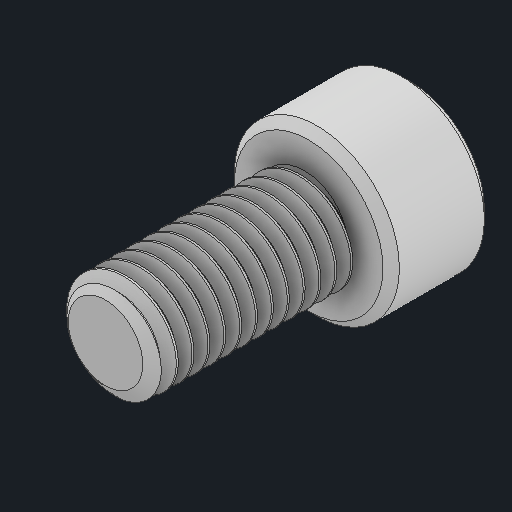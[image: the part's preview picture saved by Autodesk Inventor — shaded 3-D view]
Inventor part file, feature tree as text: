
AUTODESK INVENTOR PART (.ipt)
format: ipt  version: 2024 (Build 280153000, 153)  size: 544,768 bytes
history: native  units: in
note: dims shown in document units (in); Inventor stores cm internally (conversion verified against a paired STEP export)
features: chamfer x1
ambient origin geometry x8: Origin, YZ Plane, XZ Plane, XY Plane, X Axis, Y Axis, Z Axis, Center Point
bodies: Solid1 (feature_tree)
feature tree (1):
  chamfer  "Chamfer1"  [1 undecoded]
note: 1 required parameter value undecoded (feature->parameter linkage not recoverable at this tier; creation-order binding heuristic only, values carry confidence <= 0.55)
